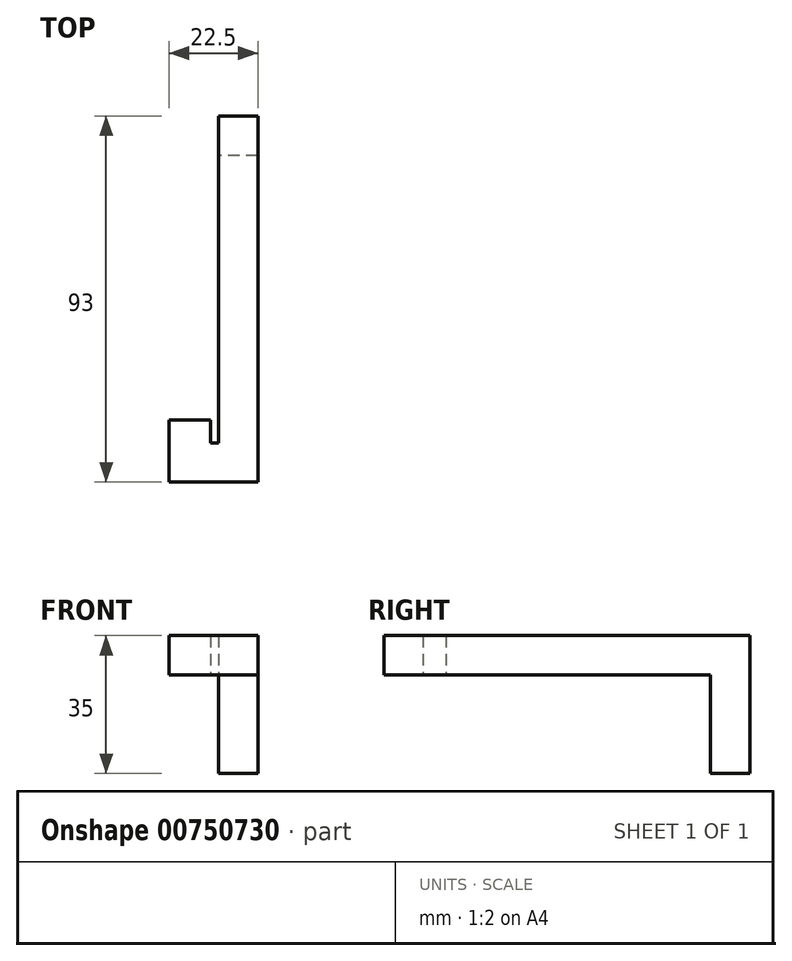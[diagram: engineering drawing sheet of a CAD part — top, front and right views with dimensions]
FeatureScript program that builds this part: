
annotation { "Feature Type Name" : "Feature", "Feature Type Description" : "" }
export const myFeature = defineFeature(function(context is Context, id is Id, definition is map)
    precondition{}
    {
        {
            var Q0;
            Q0=qCreatedBy(makeId("Top.planeOp"),FACE);
            var sketch = newSketch(context, id + "F0", { "sketchPlane" : qUnion([Q0])});
            skPoint(sketch, "E0.middle", {"position": v(0, 0) * mm});
            skLineSegment(sketch, "E1", {"start": v(22.5, 93) * mm, "end": v(22.5, 0) * mm});
            skLineSegment(sketch, "E2", {"start": v(22.5, 0) * mm, "end": v(0, 0) * mm});
            skLineSegment(sketch, "E3", {"start": v(12.5, 10) * mm, "end": v(12.5, 93) * mm});
            skLineSegment(sketch, "E4", {"start": v(12.5, 10) * mm, "end": v(10.5, 10) * mm});
            skLineSegment(sketch, "E5", {"start": v(10.5, 10) * mm, "end": v(10.5, 15.8) * mm});
            skLineSegment(sketch, "E6", {"start": v(10.5, 15.8) * mm, "end": v(0, 15.8) * mm});
            skLineSegment(sketch, "E7", {"start": v(0, 15.8) * mm, "end": v(0, 0) * mm});
            skLineSegment(sketch, "E8", {"start": v(11.5, 10) * mm, "end": v(11.5, 0) * mm, "construction": true});
            skLineSegment(sketch, "E9", {"start": v(22.5, 93) * mm, "end": v(12.5, 93) * mm});
            skSolve(sketch);
        }
        {
            var Q0;
            Q0=qSketchRegion(id+"F0",true);
            extrude(context, id + "F1", {"entities" : qUnion([Q0]), "endBound" : BoundingType.SYMMETRIC, "depth" : 10 * mm, "offsetDistance" : 25 * mm});
        }
        {
            var Q0;
            Q0=makeQuery(id+"F1.opExtrude","CAP_FACE",FACE,{"disambiguationData":[OSD([sQuery(id+"F0.wireOp",EDGE,"E1"),sQuery(id+"F0.wireOp",EDGE,"E2"),sQuery(id+"F0.wireOp",EDGE,"E3"),sQuery(id+"F0.wireOp",EDGE,"E4"),sQuery(id+"F0.wireOp",EDGE,"E5"),sQuery(id+"F0.wireOp",EDGE,"E6"),sQuery(id+"F0.wireOp",EDGE,"E7"),sQuery(id+"F0.wireOp",EDGE,"E9")])],"isStart":true});
            var sketch = newSketch(context, id + "F2", { "sketchPlane" : qUnion([Q0])});
            skLineSegment(sketch, "E10.bottom", {"start": v(22.5, -93) * mm, "end": v(12.5, -93) * mm});
            skLineSegment(sketch, "E10.top", {"start": v(22.5, -83) * mm, "end": v(12.5, -83) * mm});
            skLineSegment(sketch, "E10.left", {"start": v(22.5, -93) * mm, "end": v(22.5, -83) * mm});
            skLineSegment(sketch, "E10.right", {"start": v(12.5, -93) * mm, "end": v(12.5, -83) * mm});
            skSolve(sketch);
        }
        {
            var Q0;
            Q0=qSketchRegion(id+"F2",true);
            extrude(context, id + "F3", {"entities" : qUnion([Q0]), "operationType" : NewBodyOperationType.ADD, "depth" : 25 * mm, "offsetDistance" : 25 * mm});
        }
    });
